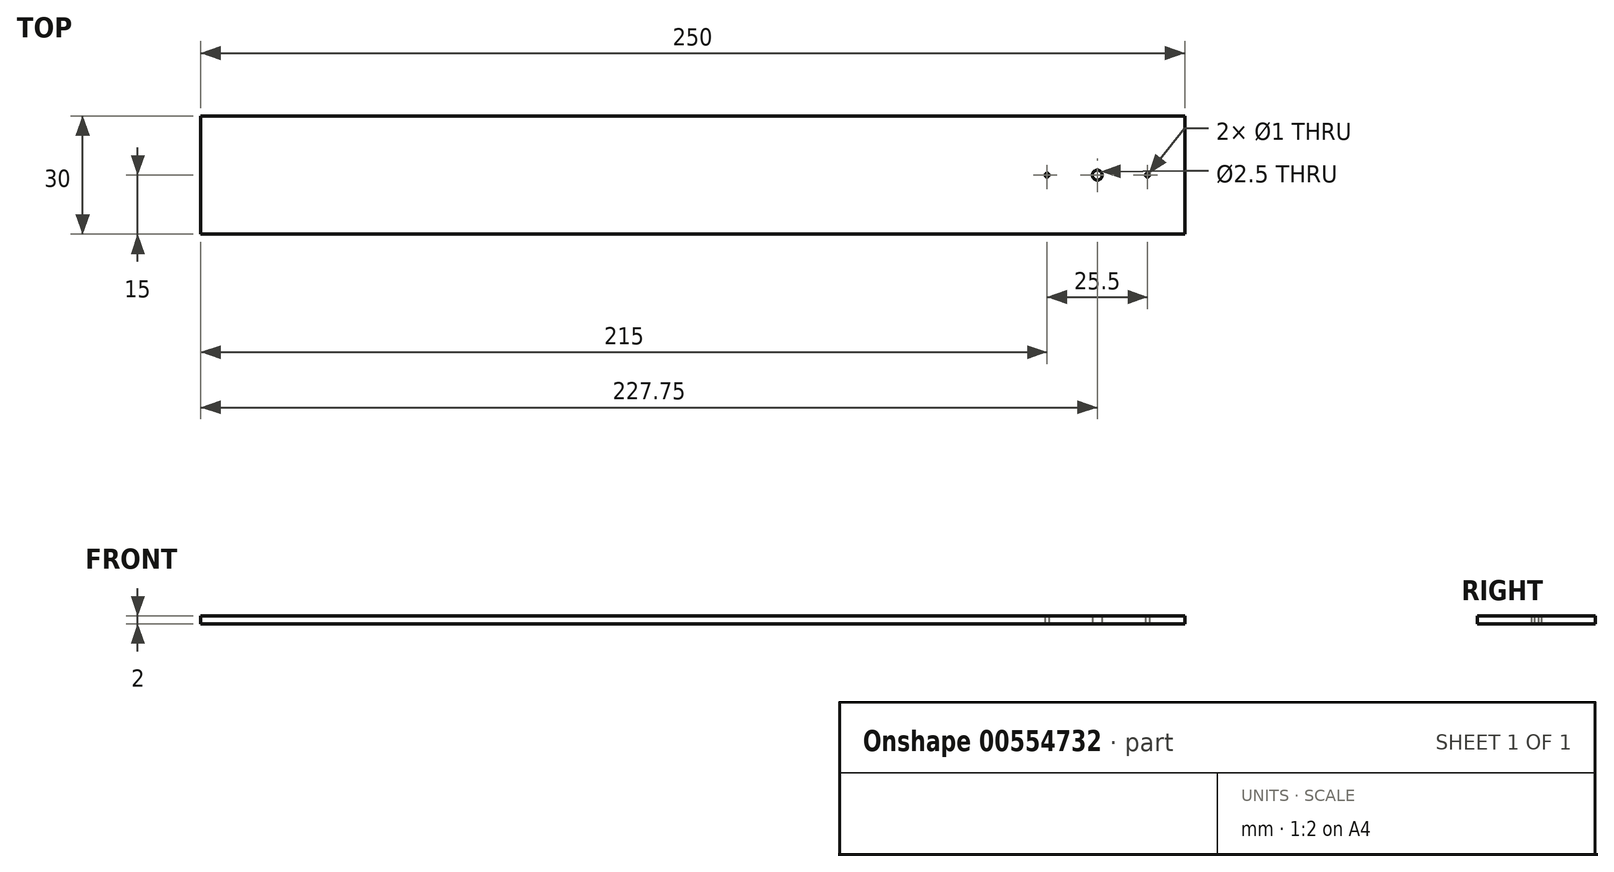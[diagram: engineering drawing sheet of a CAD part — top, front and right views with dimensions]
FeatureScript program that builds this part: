
annotation { "Feature Type Name" : "Feature", "Feature Type Description" : "" }
export const myFeature = defineFeature(function(context is Context, id is Id, definition is map)
    precondition{}
    {
        {
            var Q0;
            Q0=qCreatedBy(makeId("Top.planeOp"),FACE);
            var sketch = newSketch(context, id + "F0", { "sketchPlane" : qUnion([Q0])});
            skLineSegment(sketch, "E0.bottom", {"start": v(125, 15) * mm, "end": v(-125, 15) * mm});
            skLineSegment(sketch, "E0.top", {"start": v(125, -15) * mm, "end": v(-125, -15) * mm});
            skLineSegment(sketch, "E0.left", {"start": v(125, 15) * mm, "end": v(125, -15) * mm});
            skLineSegment(sketch, "E0.right", {"start": v(-125, 15) * mm, "end": v(-125, -15) * mm});
            skPoint(sketch, "E0.middle", {"position": v(0, 0) * mm});
            skPoint(sketch, "E1", {"position": v(90, 0) * mm});
            skPoint(sketch, "E2", {"position": v(115.5, 0) * mm});
            skPoint(sketch, "E3", {"position": v(102.75, 0) * mm});
            skCircle(sketch, "E4", {"center": v(102.75, 0) * mm, "radius": 1.25 * mm});
            skCircle(sketch, "E5", {"center": v(90, 0) * mm, "radius": 0.5 * mm});
            skCircle(sketch, "E6", {"center": v(115.5, 0) * mm, "radius": 0.5 * mm});
            skSolve(sketch);
        }
        {
            var Q0;
            Q0=makeQuery(id+"F0.imprint","IMPRINT",FACE,{"disambiguationData":[TD([[makeQuery(id+"F0.imprint","IMPRINT",EDGE,{"derivedFrom":sQuery(id+"F0.wireOp",EDGE,"E0.bottom")}),1.0]])]});
            extrude(context, id + "F1", {"entities" : qUnion([Q0]), "endBound" : BoundingType.SYMMETRIC, "depth" : 2 * mm, "offsetDistance" : 25 * mm});
        }
    });
